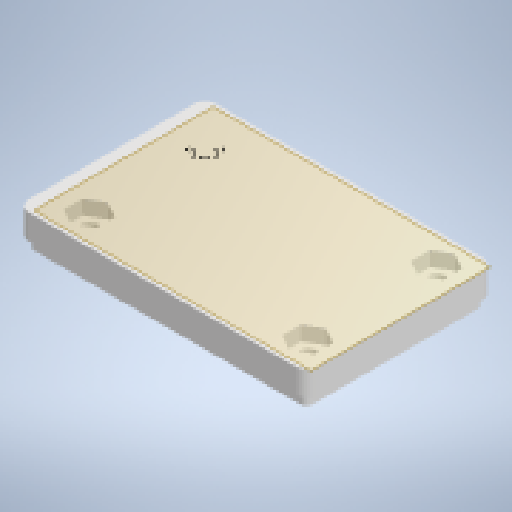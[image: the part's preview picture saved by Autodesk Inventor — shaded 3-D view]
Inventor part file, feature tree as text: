
AUTODESK INVENTOR PART (.ipt)
format: ipt  version: 2024 (Build 280153000, 153)  size: 298,496 bytes
history: native  units: mm
features: extrude x8, sketch x8, projected_geometry x6, reference x5, other x4, plane x3, fillet x2
ambient origin geometry x8: Origin, YZ Plane, XZ Plane, XY Plane, X Axis, Y Axis, Z Axis, Center Point
bodies: Body1 (feature_tree)
feature tree (36):
  plane  "Arbeitsebene1"
  extrude  "Extrusion2"  Depth=2.6mm
  sketch  "Skizze4"  dims[d7=2.0mm d8=0.0mm d9=2.0mm]
  plane  "Arbeitsebene2"
  extrude  "Extrusion3"  Depth=2.0mm
  extrude  "Extrusion4"  Depth=1.0mm
  sketch  "Skizze6"  dims[d13=2.0mm d14=0.0mm d15=0.2mm]
  plane  "Arbeitsebene3"
  extrude  "Extrusion5"  Depth=0.2mm
  extrude  "Extrusion6"  Depth=0.2mm
  extrude  "Extrusion7"  Depth=6.6mm
  fillet  "Rundung1"  Radius=2.0mm
  fillet  "Rundung2"  Radius=6.2mm
  extrude  "Extrusion8"  Depth=6.6mm
  extrude  "Extrusion9"  Depth=2.0mm
  sketch  "Skizze3"  dims[d5=2.2mm d6=2.6mm]
  reference  "Referenz3"
  reference  "Referenz4"
  projected_geometry  "Projizierte Kontur2"
  sketch  "Skizze5"  dims[d10=2.0mm d11=0.0mm d12=1.0mm]
  projected_geometry  "Projizierte Kontur3"
  reference  "Referenz5"
  reference  "Referenz6"
  reference  "Referenz7"
  sketch  "Skizze7"  dims[d16=0.2mm d17=0.2mm]
  projected_geometry  "Projizierte Kontur4"
  projected_geometry  "Projizierte Kontur5"
  projected_geometry  "Projizierte Kontur6"
  sketch  "Skizze8"  dims[d18=6.2mm d19=6.6mm d20=2.0mm d21=6.2mm]
  projected_geometry  "Projizierte Kontur7"
  sketch  "Skizze9"  dims[d22=6.6mm d23=3.3mm]
  sketch  "Skizze10"  dims[d24=3.1mm d25=2.0mm d26=2.0mm d27=2.211mm d28=0.0mm d29=2.8mm d30=0.0mm d31=5.7mm d32=5.7mm d33=5.7mm d34=2.6mm d35=0.0mm d36=2.0mm d37=1.0mm d38=3.3mm d39=3.3mm d40=10.0mm d41=0.0mm d42=5.7mm d43=2.6mm d44=0.0mm]
  parser-record x1  (decoder bookkeeping rows leaked as tree rows — omitted from the tree; the rows remain in map.json)
  other  "main.iam"
  other  "Umgebungssensor_PCB:1"
  other  "GY-BME280:1"
note: 1 file-system path scrubbed to <path> (originals preserved in map.json)
